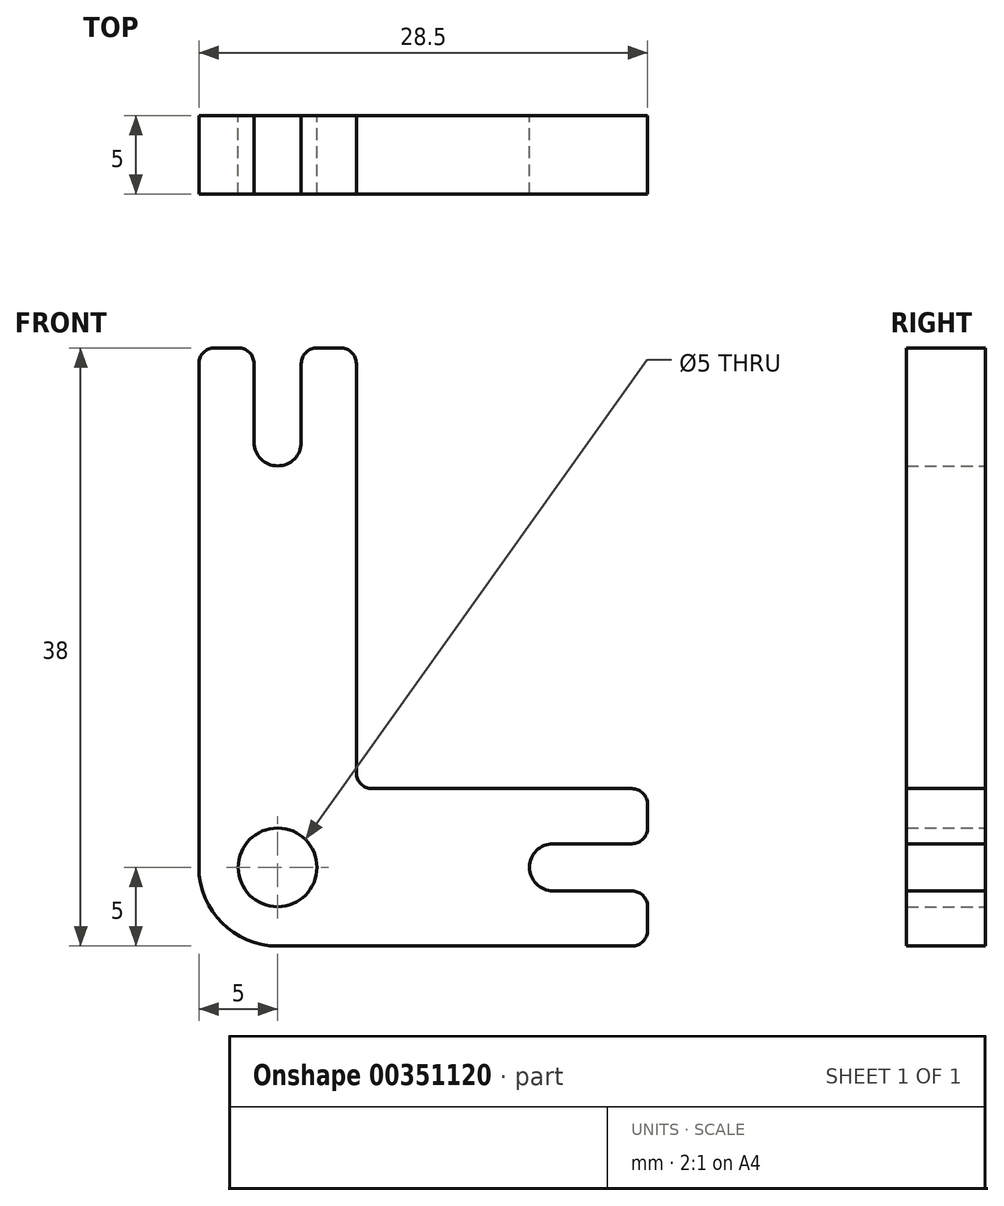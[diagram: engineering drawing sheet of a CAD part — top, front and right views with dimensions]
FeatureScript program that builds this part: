
annotation { "Feature Type Name" : "Feature", "Feature Type Description" : "" }
export const myFeature = defineFeature(function(context is Context, id is Id, definition is map)
    precondition{}
    {
        {
            var Q0;
            Q0=qCreatedBy(makeId("Front.planeOp"),FACE);
            var sketch = newSketch(context, id + "F0", { "sketchPlane" : qUnion([Q0])});
            skLineSegment(sketch, "E0", {"start": v(0, 17.27) * mm, "end": v(0, -21.4) * mm, "construction": true});
            skLineSegment(sketch, "E1", {"start": v(-23.05, 0) * mm, "end": v(27.97, 0) * mm, "construction": true});
            skLineSegment(sketch, "E2.bottom", {"start": v(-4, 33) * mm, "end": v(-2.5, 33) * mm});
            skLineSegment(sketch, "E2.left", {"start": v(-5, 32) * mm, "end": v(-5, 0) * mm});
            skLineSegment(sketch, "E2.right", {"start": v(5, 32) * mm, "end": v(5, 6) * mm});
            skLineSegment(sketch, "E3.bottom", {"start": v(0, -5) * mm, "end": v(22.5, -5) * mm});
            skLineSegment(sketch, "E3.right", {"start": v(23.5, -4) * mm, "end": v(23.5, -2.5) * mm});
            skLineSegment(sketch, "E4.trimOffspring", {"start": v(6, 5) * mm, "end": v(22.5, 5) * mm});
            skCircle(sketch, "E5", {"center": v(0, 0) * mm, "radius": 2.5 * mm});
            skLineSegment(sketch, "E6", {"start": v(-1.5, 32) * mm, "end": v(-1.5, 27) * mm});
            skLineSegment(sketch, "E7", {"start": v(1.5, 27) * mm, "end": v(1.5, 32) * mm});
            skLineSegment(sketch, "E8.trimOffspring", {"start": v(2.5, 33) * mm, "end": v(4, 33) * mm});
            skArc(sketch, "E9", {"start": v(-1.5, 27) * mm, "mid": v(0, 25.5) * mm, "end": v(1.5, 27) * mm});
            skLineSegment(sketch, "E10", {"start": v(22.5, 1.5) * mm, "end": v(17.5, 1.5) * mm});
            skLineSegment(sketch, "E11", {"start": v(17.5, -1.5) * mm, "end": v(22.5, -1.5) * mm});
            skLineSegment(sketch, "E12.trimOffspring", {"start": v(23.5, 2.5) * mm, "end": v(23.5, 4) * mm});
            skArc(sketch, "E13", {"start": v(17.5, -1.5) * mm, "mid": v(16, 0) * mm, "end": v(17.5, 1.5) * mm});
            skPoint(sketch, "E14.visualSharp", {"position": v(-5, -5) * mm});
            skArc(sketch, "E14.filletArc", {"start": v(-5, 0) * mm, "mid": v(-3.54, -3.54) * mm, "end": v(0, -5) * mm});
            skPoint(sketch, "E15.visualSharp", {"position": v(5, 5) * mm});
            skArc(sketch, "E15.filletArc", {"start": v(5, 6) * mm, "mid": v(5.3, 5.3) * mm, "end": v(6, 5) * mm});
            skPoint(sketch, "E16.visualSharp", {"position": v(-5, 33) * mm});
            skArc(sketch, "E16.filletArc", {"start": v(-4, 33) * mm, "mid": v(-4.7, 32.7) * mm, "end": v(-5, 32) * mm});
            skPoint(sketch, "E17.visualSharp", {"position": v(5, 33) * mm});
            skArc(sketch, "E17.filletArc", {"start": v(5, 32) * mm, "mid": v(4.7, 32.7) * mm, "end": v(4, 33) * mm});
            skPoint(sketch, "E18.visualSharp", {"position": v(23.5, 5) * mm});
            skArc(sketch, "E18.filletArc", {"start": v(23.5, 4) * mm, "mid": v(23.2, 4.7) * mm, "end": v(22.5, 5) * mm});
            skPoint(sketch, "E19.visualSharp", {"position": v(23.5, -5) * mm});
            skArc(sketch, "E19.filletArc", {"start": v(22.5, -5) * mm, "mid": v(23.2, -4.7) * mm, "end": v(23.5, -4) * mm});
            skPoint(sketch, "E20.visualSharp", {"position": v(-1.5, 33) * mm});
            skArc(sketch, "E20.filletArc", {"start": v(-1.5, 32) * mm, "mid": v(-1.8, 32.7) * mm, "end": v(-2.5, 33) * mm});
            skPoint(sketch, "E21.visualSharp", {"position": v(1.5, 33) * mm});
            skArc(sketch, "E21.filletArc", {"start": v(2.5, 33) * mm, "mid": v(1.8, 32.7) * mm, "end": v(1.5, 32) * mm});
            skPoint(sketch, "E22.visualSharp", {"position": v(23.5, 1.5) * mm});
            skArc(sketch, "E22.filletArc", {"start": v(22.5, 1.5) * mm, "mid": v(23.2, 1.8) * mm, "end": v(23.5, 2.5) * mm});
            skPoint(sketch, "E23.visualSharp", {"position": v(23.5, -1.5) * mm});
            skArc(sketch, "E23.filletArc", {"start": v(23.5, -2.5) * mm, "mid": v(23.2, -1.8) * mm, "end": v(22.5, -1.5) * mm});
            skSolve(sketch);
        }
        {
            var Q0;
            Q0=makeQuery(id+"F0.imprint","IMPRINT",FACE,{"disambiguationData":[TD([[makeQuery(id+"F0.imprint","IMPRINT",EDGE,{"derivedFrom":sQuery(id+"F0.wireOp",EDGE,"E2.bottom")}),-1.0]])]});
            extrude(context, id + "F1", {"entities" : qUnion([Q0]), "depth" : 5 * mm});
        }
    });
